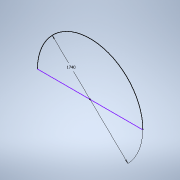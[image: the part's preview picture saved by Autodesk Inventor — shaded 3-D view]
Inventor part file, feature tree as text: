
AUTODESK INVENTOR PART (.ipt)
format: ipt  version: 2021 (Build 250183000, 183)  size: 108,544 bytes
history: native  units: mm
features: other x3, chamfer x1, sketch x1
ambient origin geometry x8: Origin, YZ Plane, XZ Plane, XY Plane, X Axis, Y Axis, Z Axis, Center Point
bodies: Body1 (feature_tree)
feature tree (5):
  other  "Bryła1"
  other  "Powierzchnia1"
  chamfer  "Faza1"  Distance=1740.0mm
  sketch  "Szkic1"
  other  "Płyta1"
